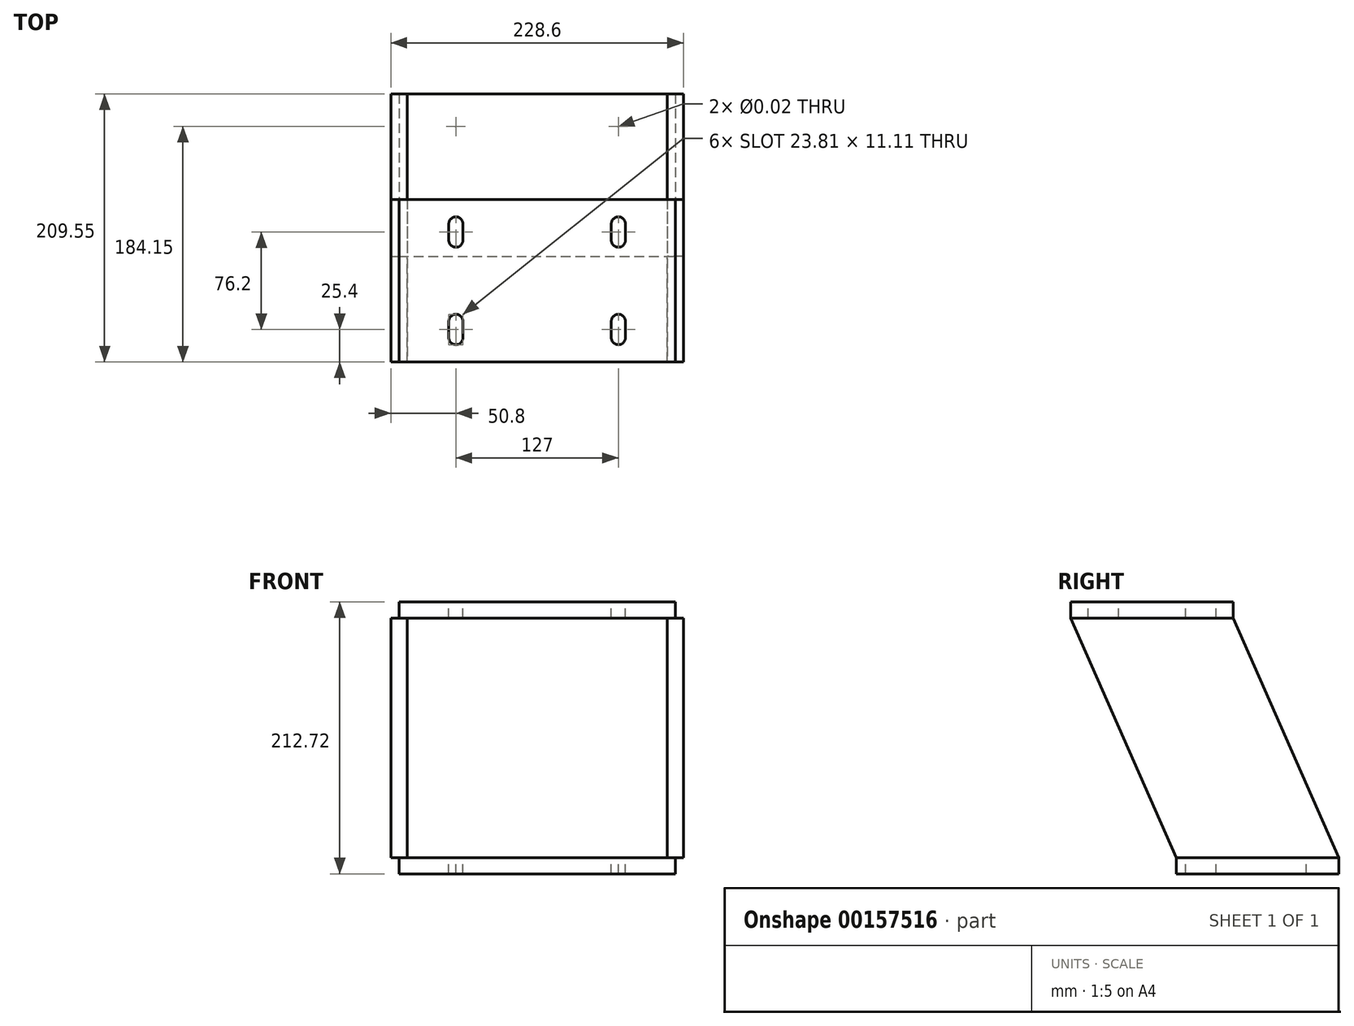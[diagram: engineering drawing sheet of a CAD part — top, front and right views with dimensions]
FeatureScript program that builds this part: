
annotation { "Feature Type Name" : "Feature", "Feature Type Description" : "" }
export const myFeature = defineFeature(function(context is Context, id is Id, definition is map)
    precondition{}
    {
        {
            var Q0;
            Q0=qCreatedBy(makeId("Top.planeOp"),FACE);
            var sketch = newSketch(context, id + "F0", { "sketchPlane" : qUnion([Q0])});
            skLineSegment(sketch, "E0.bottom", {"start": v(-107.95, 63.5) * mm, "end": v(107.95, 63.5) * mm});
            skLineSegment(sketch, "E0.top", {"start": v(-107.95, -63.5) * mm, "end": v(107.95, -63.5) * mm});
            skLineSegment(sketch, "E0.left", {"start": v(-107.95, 63.5) * mm, "end": v(-107.95, -63.5) * mm});
            skLineSegment(sketch, "E0.right", {"start": v(107.95, 63.5) * mm, "end": v(107.95, -63.5) * mm});
            skPoint(sketch, "E0.middle", {"position": v(0, 0) * mm});
            skSolve(sketch);
        }
        {
            var Q0;
            Q0 = qSketchRegion(id + "F0", true);
            extrude(context, id + "F1", {"entities" : qUnion([Q0]), "depth" : 12.7 * mm});
        }
        {
            var Q0;
            Q0=makeQuery(id+"F1.opExtrude","CAP_FACE",FACE,{"disambiguationData":[OSD([sQuery(id+"F0.wireOp",EDGE,"E0.bottom"),sQuery(id+"F0.wireOp",EDGE,"E0.top"),sQuery(id+"F0.wireOp",EDGE,"E0.left"),sQuery(id+"F0.wireOp",EDGE,"E0.right")])],"isStart":false});
            var sketch = newSketch(context, id + "F2", { "sketchPlane" : qUnion([Q0])});
            skLineSegment(sketch, "E1.bottom", {"start": v(-63.5, 38.1) * mm, "end": v(63.5, 38.1) * mm, "construction": true});
            skLineSegment(sketch, "E1.top", {"start": v(-63.5, -38.1) * mm, "end": v(63.5, -38.1) * mm, "construction": true});
            skLineSegment(sketch, "E1.left", {"start": v(-63.5, 38.1) * mm, "end": v(-63.5, -38.1) * mm, "construction": true});
            skLineSegment(sketch, "E1.right", {"start": v(63.5, 38.1) * mm, "end": v(63.5, -38.1) * mm, "construction": true});
            skPoint(sketch, "E1.middle", {"position": v(0, 0) * mm});
            skPoint(sketch, "E2", {"position": v(-63.5, 38.1) * mm});
            skPoint(sketch, "E3", {"position": v(63.5, 38.1) * mm});
            skPoint(sketch, "E4", {"position": v(63.5, -38.1) * mm});
            skPoint(sketch, "E5", {"position": v(-63.5, -38.1) * mm});
            skSolve(sketch);
        }
        {
            var Q0;
            Q0=sQuery(id+"F2.wireOp",VERTEX,"E2");
            var Q1;
            Q1=sQuery(id+"F2.wireOp",VERTEX,"E3");
            var Q2;
            Q2=sQuery(id+"F2.wireOp",VERTEX,"E4");
            var Q3;
            Q3=sQuery(id+"F2.wireOp",VERTEX,"E5");
            var Q4;
            Q4=makeQuery(id+"F1.opExtrude","SWEPT_BODY",BODY,{"disambiguationData":[OSD([sQuery(id+"F0.wireOp",EDGE,"E0.bottom"),sQuery(id+"F0.wireOp",EDGE,"E0.top"),sQuery(id+"F0.wireOp",EDGE,"E0.left"),sQuery(id+"F0.wireOp",EDGE,"E0.right")])]});
            hole(context, id + "F3", {"style" : HoleStyle.SIMPLE, "endStyle" : HoleEndStyle.THROUGH, "standardTappedOrClearance" : lookupTablePath({ "standard" : "ANSI", "size" : "9/16 (0.56)", "type" : "Drilled" }), "standardBlindInLast" : lookupTablePath({ "standard" : "ANSI", "size" : "9/16", "type" : "Drilled" }), "holeDiameter" : 9 / 406.4 * mm, "locations" : qUnion([Q0, Q1, Q2, Q3]), "scope" : qUnion([Q4]), "isTappedThrough" : true});
        }
        {
            var Q0;
            Q0=qCreatedBy(makeId("Top.planeOp"),FACE);
            cPlane(context, id + "F4", {"entities" : qUnion([Q0]), "cplaneType" : CPlaneType.OFFSET, "offset" : 212.72 * mm, "width" : 152.4 * mm, "height" : 152.4 * mm});
        }
        {
            var Q0;
            Q0=qCreatedBy(id+"F4.planeOp",FACE);
            var sketch = newSketch(context, id + "F5", { "sketchPlane" : qUnion([Q0])});
            skLineSegment(sketch, "E6.0", {"start": v(-107.95, 63.5) * mm, "end": v(107.95, 63.5) * mm, "construction": true});
            skLineSegment(sketch, "E7.0", {"start": v(-107.95, -19.05) * mm, "end": v(107.95, -19.05) * mm, "construction": true});
            skLineSegment(sketch, "E8.bottom", {"start": v(-107.95, -19.05) * mm, "end": v(107.95, -19.05) * mm});
            skLineSegment(sketch, "E8.top", {"start": v(-107.95, -146.05) * mm, "end": v(107.95, -146.05) * mm});
            skLineSegment(sketch, "E8.left", {"start": v(-107.95, -19.05) * mm, "end": v(-107.95, -146.05) * mm});
            skLineSegment(sketch, "E8.right", {"start": v(107.95, -19.05) * mm, "end": v(107.95, -146.05) * mm});
            skSolve(sketch);
        }
        {
            var Q0;
            Q0 = qSketchRegion(id + "F5", true);
            extrude(context, id + "F6", {"entities" : qUnion([Q0]), "oppositeDirection" : true, "depth" : 12.7 * mm});
        }
        {
            var Q0;
            Q0=makeQuery(id+"F6.opExtrude","CAP_FACE",FACE,{"disambiguationData":[OSD([sQuery(id+"F5.wireOp",EDGE,"E8.bottom"),sQuery(id+"F5.wireOp",EDGE,"E8.top"),sQuery(id+"F5.wireOp",EDGE,"E8.left"),sQuery(id+"F5.wireOp",EDGE,"E8.right")])],"isStart":true});
            var sketch = newSketch(context, id + "F7", { "sketchPlane" : qUnion([Q0])});
            skPoint(sketch, "E9.0", {"position": v(-107.95, -63.5) * mm});
            skLineSegment(sketch, "E10.0", {"start": v(-107.95, -19.05) * mm, "end": v(-107.95, -146.05) * mm, "construction": true});
            skLineSegment(sketch, "E11.0", {"start": v(107.95, -19.05) * mm, "end": v(107.95, -146.05) * mm, "construction": true});
            skLineSegment(sketch, "E12", {"start": v(-107.95, -19.05) * mm, "end": v(107.95, -146.05) * mm, "construction": true});
            skLineSegment(sketch, "E13", {"start": v(107.95, -19.05) * mm, "end": v(-107.95, -146.05) * mm, "construction": true});
            skLineSegment(sketch, "E14.bottom", {"start": v(-63.5, -44.45) * mm, "end": v(63.5, -44.45) * mm, "construction": true});
            skLineSegment(sketch, "E14.top", {"start": v(-63.5, -120.65) * mm, "end": v(63.5, -120.65) * mm, "construction": true});
            skLineSegment(sketch, "E14.left", {"start": v(-63.5, -44.45) * mm, "end": v(-63.5, -120.65) * mm, "construction": true});
            skLineSegment(sketch, "E14.right", {"start": v(63.5, -44.45) * mm, "end": v(63.5, -120.65) * mm, "construction": true});
            skPoint(sketch, "E14.middle", {"position": v(0, -82.55) * mm});
            skPoint(sketch, "E15", {"position": v(-63.5, -44.45) * mm});
            skPoint(sketch, "E16", {"position": v(63.5, -44.45) * mm});
            skPoint(sketch, "E17", {"position": v(63.5, -120.65) * mm});
            skPoint(sketch, "E18", {"position": v(-63.5, -120.65) * mm});
            skLineSegment(sketch, "E19", {"start": v(-63.5, -38.1) * mm, "end": v(-63.5, -50.8) * mm});
            skArc(sketch, "E20.0.startCap", {"start": v(-69.06, -38.1) * mm, "mid": v(-63.5, -32.54) * mm, "end": v(-57.94, -38.1) * mm});
            skArc(sketch, "E20.0.endCap", {"start": v(-57.94, -50.8) * mm, "mid": v(-63.5, -56.36) * mm, "end": v(-69.06, -50.8) * mm});
            skLineSegment(sketch, "E20.0.left", {"start": v(-57.94, -38.1) * mm, "end": v(-57.94, -50.8) * mm});
            skLineSegment(sketch, "E20.0.right", {"start": v(-69.06, -38.1) * mm, "end": v(-69.06, -50.8) * mm});
            skLineSegment(sketch, "E21.0.1.1", {"start": v(-63.5, -114.3) * mm, "end": v(-63.5, -127) * mm});
            skArc(sketch, "E21.0.1.2", {"start": v(-69.06, -114.3) * mm, "mid": v(-63.5, -108.74) * mm, "end": v(-57.94, -114.3) * mm});
            skArc(sketch, "E21.0.1.3", {"start": v(-57.94, -127) * mm, "mid": v(-63.5, -132.56) * mm, "end": v(-69.06, -127) * mm});
            skLineSegment(sketch, "E21.0.1.4", {"start": v(-57.94, -114.3) * mm, "end": v(-57.94, -127) * mm});
            skLineSegment(sketch, "E21.0.1.5", {"start": v(-69.06, -114.3) * mm, "end": v(-69.06, -127) * mm});
            skLineSegment(sketch, "E21.1.0.1", {"start": v(63.5, -38.1) * mm, "end": v(63.5, -50.8) * mm});
            skArc(sketch, "E21.1.0.2", {"start": v(57.94, -38.1) * mm, "mid": v(63.5, -32.54) * mm, "end": v(69.06, -38.1) * mm});
            skArc(sketch, "E21.1.0.3", {"start": v(69.06, -50.8) * mm, "mid": v(63.5, -56.36) * mm, "end": v(57.94, -50.8) * mm});
            skLineSegment(sketch, "E21.1.0.4", {"start": v(69.06, -38.1) * mm, "end": v(69.06, -50.8) * mm});
            skLineSegment(sketch, "E21.1.0.5", {"start": v(57.94, -38.1) * mm, "end": v(57.94, -50.8) * mm});
            skLineSegment(sketch, "E21.1.1.1", {"start": v(63.5, -114.3) * mm, "end": v(63.5, -127) * mm});
            skArc(sketch, "E21.1.1.2", {"start": v(57.94, -114.3) * mm, "mid": v(63.5, -108.74) * mm, "end": v(69.06, -114.3) * mm});
            skArc(sketch, "E21.1.1.3", {"start": v(69.06, -127) * mm, "mid": v(63.5, -132.56) * mm, "end": v(57.94, -127) * mm});
            skLineSegment(sketch, "E21.1.1.4", {"start": v(69.06, -114.3) * mm, "end": v(69.06, -127) * mm});
            skLineSegment(sketch, "E21.1.1.5", {"start": v(57.94, -114.3) * mm, "end": v(57.94, -127) * mm});
            skLineSegment(sketch, "E21.direction1", {"start": v(-69.06, -50.8) * mm, "end": v(57.94, -50.8) * mm, "construction": true});
            skLineSegment(sketch, "E21.direction2", {"start": v(-69.06, -50.8) * mm, "end": v(-69.06, -127) * mm, "construction": true});
            skSolve(sketch);
        }
        {
            var Q0;
            Q0 = qSketchRegion(id + "F7", true);
            extrude(context, id + "F8", {"entities" : qUnion([Q0]), "operationType" : NewBodyOperationType.REMOVE, "endBound" : BoundingType.THROUGH_ALL, "oppositeDirection" : true, "depth" : 25.4 * mm});
        }
        {
            var Q0;
            Q0=makeQuery(id+"F6.opExtrude","SWEPT_FACE",FACE,{"disambiguationData":[OSD([sQuery(id+"F5.wireOp",EDGE,"E8.right")])]});
            var sketch = newSketch(context, id + "F9", { "sketchPlane" : qUnion([Q0])});
            skLineSegment(sketch, "E22.0", {"start": v(-19.05, 200.03) * mm, "end": v(-146.05, 200.03) * mm});
            skLineSegment(sketch, "E23.0", {"start": v(63.5, 12.7) * mm, "end": v(-63.5, 12.7) * mm});
            skLineSegment(sketch, "E24", {"start": v(-146.05, 200.02) * mm, "end": v(-63.5, 12.7) * mm});
            skLineSegment(sketch, "E25", {"start": v(-19.05, 200.03) * mm, "end": v(63.5, 12.7) * mm});
            skSolve(sketch);
        }
        {
            var Q0;
            Q0 = qSketchRegion(id + "F9", true);
            extrude(context, id + "F10", {"entities" : qUnion([Q0]), "endBound" : BoundingType.SYMMETRIC, "depth" : 12.7 * mm});
        }
        {
            var Q0;
            Q0=makeQuery(id+"F10.opExtrude","SWEPT_BODY",BODY,{"disambiguationData":[OSD([sQuery(id+"F9.wireOp",EDGE,"E22.0"),sQuery(id+"F9.wireOp",EDGE,"E23.0"),sQuery(id+"F9.wireOp",EDGE,"E24"),sQuery(id+"F9.wireOp",EDGE,"E25")])]});
            var Q1;
            Q1=qCreatedBy(makeId("Right.planeOp"),FACE);
            mirror(context, id + "F11", {"entities" : qUnion([Q0]), "mirrorPlane" : qUnion([Q1])});
        }
    });
